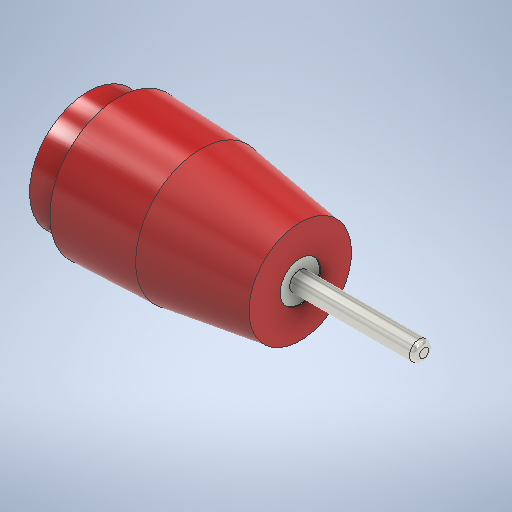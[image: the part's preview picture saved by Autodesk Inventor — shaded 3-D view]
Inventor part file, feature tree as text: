
AUTODESK INVENTOR PART (.ipt)
format: ipt  version: 2025 (Build 290162000, 162)  size: 295,936 bytes
history: native  units: in
note: dims shown in document units (in); Inventor stores cm internally (conversion verified against a paired STEP export)
features: sketch x3, extrude x2, revolve x1
ambient origin geometry x8: Origin, YZ Plane, XZ Plane, XY Plane, X Axis, Y Axis, Z Axis, Center Point
bodies: Solid1 (feature_tree)
feature tree (6):
  revolve  "Revolution1"  [1 undecoded]
  extrude  "Extrusion1"  Depth=0.7087in
  extrude  "Extrusion2"  Depth=0.0197in
  sketch  "Sketch1"  dims[d0=0.2264in d1=0.1181in]
  sketch  "Sketch2"  dims[d2=0.0394in d3=0.7087in]
  sketch  "Sketch3"  dims[d5=0.4803in d6=0.0197in d7=90.0deg d8=0.1575in d9=0.7874in d10=0.0in d11=0.0374in d12=0.1575in d13=0.0039in d14=0.0in]
note: 1 required parameter value undecoded (feature->parameter linkage not recoverable at this tier; creation-order binding heuristic only, values carry confidence <= 0.55)
